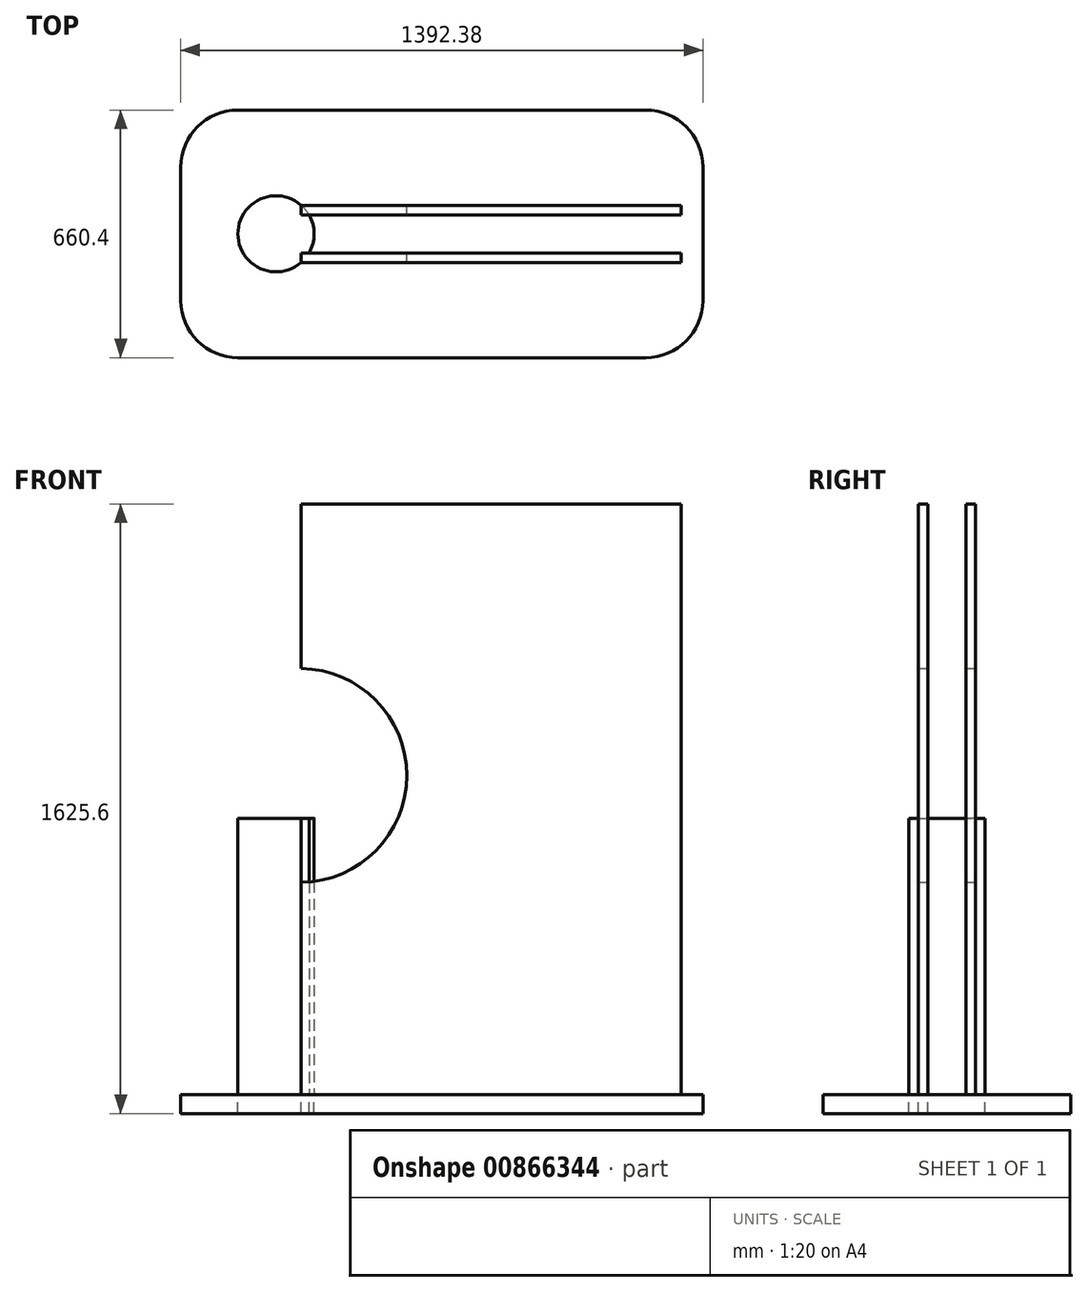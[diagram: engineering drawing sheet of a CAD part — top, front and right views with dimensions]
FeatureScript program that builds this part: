
annotation { "Feature Type Name" : "Feature", "Feature Type Description" : "" }
export const myFeature = defineFeature(function(context is Context, id is Id, definition is map)
    precondition{}
    {
        {
            var Q0;
            Q0=qCreatedBy(makeId("Front.planeOp"),FACE);
            var sketch = newSketch(context, id + "F1", { "sketchPlane" : qUnion([Q0])});
            skArc(sketch, "E0", {"start": v(32.8, 565.52) * mm, "mid": v(314.4, 850.7) * mm, "end": v(32.8, 1135.86) * mm});
            skLineSegment(sketch, "E1.bottom", {"start": v(32.8, 0) * mm, "end": v(1045.36, 0) * mm});
            skLineSegment(sketch, "E1.top", {"start": v(32.8, 1574.8) * mm, "end": v(1045.36, 1574.8) * mm});
            skLineSegment(sketch, "E1.left", {"start": v(32.8, 0) * mm, "end": v(32.8, 565.52) * mm});
            skLineSegment(sketch, "E1.right", {"start": v(1045.36, 0) * mm, "end": v(1045.36, 1574.8) * mm});
            skLineSegment(sketch, "E2.trimOffspring", {"start": v(32.8, 1135.86) * mm, "end": v(32.8, 1574.8) * mm});
            skSolve(sketch);
        }
        {
            var Q0;
            Q0=makeQuery(id+"F1.imprint","IMPRINT",FACE,{"disambiguationData":[TD([[makeQuery(id+"F1.imprint","IMPRINT",EDGE,{"derivedFrom":sQuery(id+"F1.wireOp",EDGE,"E0")}),-1.0]])]});
            extrude(context, id + "F2", {"entities" : qUnion([Q0]), "depth" : 152.4 * mm, "offsetDistance" : 25.4 * mm});
        }
        {
            var Q0;
            Q0=makeQuery(id+"F2.opExtrude","SWEPT_FACE",FACE,{"disambiguationData":[OSD([sQuery(id+"F1.wireOp",EDGE,"E1.top")])]});
            var sketch = newSketch(context, id + "F3", { "sketchPlane" : qUnion([Q0])});
            skLineSegment(sketch, "E3.bottom", {"start": v(32.8, -25.4) * mm, "end": v(1045.36, -25.4) * mm});
            skLineSegment(sketch, "E3.top", {"start": v(32.8, -127) * mm, "end": v(1045.36, -127) * mm});
            skLineSegment(sketch, "E3.left", {"start": v(32.8, -25.4) * mm, "end": v(32.8, -127) * mm});
            skLineSegment(sketch, "E3.right", {"start": v(1045.36, -25.4) * mm, "end": v(1045.36, -127) * mm});
            skSolve(sketch);
        }
        {
            var Q0;
            Q0=makeQuery(id+"F3.imprint","IMPRINT",FACE,{"disambiguationData":[TD([[makeQuery(id+"F3.imprint","IMPRINT",EDGE,{"derivedFrom":sQuery(id+"F3.wireOp",EDGE,"E3.bottom")}),-1.0]])]});
            extrude(context, id + "F4", {"entities" : qUnion([Q0]), "operationType" : NewBodyOperationType.REMOVE, "oppositeDirection" : true, "depth" : 1574.8 * mm, "offsetDistance" : 25.4 * mm});
        }
        {
            var Q0;
            {var subQ2=sQuery(id+"F1.wireOp",EDGE,"E1.bottom");Q0=makeQuery(id+"F4.boolean.opBoolean","SPLIT",FACE,{"disambiguationData":[TD([makeQuery(id+"F4.opExtrude","SWEPT_FACE",FACE,{"disambiguationData":[OSD([sQuery(id+"F3.wireOp",EDGE,"E3.top")])]})])],"derivedFrom":makeQuery(id+"F2.opExtrude","SWEPT_FACE",FACE,{"disambiguationData":[OSD([subQ2])]})});}
            var sketch = newSketch(context, id + "F5", { "sketchPlane" : qUnion([Q0])});
            skArc(sketch, "E4", {"start": v(32.8, 152.4) * mm, "mid": v(-136, 76.2) * mm, "end": v(32.8, 0) * mm});
            skCircle(sketch, "E5", {"center": v(-34.4, 76.2) * mm, "radius": 101.6 * mm});
            skSolve(sketch);
        }
        {
            var Q0;
            {var subQ1=sQuery(id+"F1.wireOp",EDGE,"E1.left");var subQ2=sQuery(id+"F1.wireOp",EDGE,"E1.bottom");var subQ3=sQuery(id+"F3.wireOp",EDGE,"E3.top");var subQ4=makeQuery(id+"F4.boolean.opBoolean","SPLIT",EDGE,{"disambiguationData":[TD([makeQuery(id+"F4.opExtrude","SWEPT_FACE",FACE,{"disambiguationData":[OSD([subQ3])]})])],"derivedFrom":makeQuery(id+"F2.opExtrude","SWEPT_EDGE",EDGE,{"disambiguationData":[OSD([subQ2,subQ1])]})});Q0=makeQuery(id+"F5.imprint","IMPRINT",FACE,{"disambiguationData":[TD([[makeQuery(id+"F5.imprint","IMPRINT",EDGE,{"derivedFrom":subQ4}),-1.0]])]});}
            extrude(context, id + "F6", {"entities" : qUnion([Q0]), "oppositeDirection" : true, "depth" : 736.6 * mm, "offsetDistance" : 25.4 * mm});
        }
        {
            var Q0;
            Q0=makeQuery(id+"F6.opExtrude","CAP_FACE",FACE,{"disambiguationData":[OSD([sQuery(id+"F1.wireOp",EDGE,"E1.bottom"),sQuery(id+"F1.wireOp",EDGE,"E1.left"),sQuery(id+"F3.wireOp",EDGE,"E3.top"),sQuery(id+"F5.wireOp",EDGE,"E5")])],"isStart":true});
            var sketch = newSketch(context, id + "F7", { "sketchPlane" : qUnion([Q0])});
            skLineSegment(sketch, "E6.bottom", {"start": v(-136, 406.4) * mm, "end": v(951.58, 406.4) * mm});
            skLineSegment(sketch, "E6.top", {"start": v(-136, -254) * mm, "end": v(951.58, -254) * mm});
            skLineSegment(sketch, "E6.left", {"start": v(-288.4, 254) * mm, "end": v(-288.4, -101.6) * mm});
            skLineSegment(sketch, "E6.right", {"start": v(1103.98, 254) * mm, "end": v(1103.98, -101.6) * mm});
            skPoint(sketch, "E7.visualSharp", {"position": v(-288.4, 406.4) * mm});
            skArc(sketch, "E7.filletArc", {"start": v(-136, 406.4) * mm, "mid": v(-243.76, 361.76) * mm, "end": v(-288.4, 254) * mm});
            skPoint(sketch, "E8.visualSharp", {"position": v(-288.4, -254) * mm});
            skArc(sketch, "E8.filletArc", {"start": v(-288.4, -101.6) * mm, "mid": v(-243.76, -209.36) * mm, "end": v(-136, -254) * mm});
            skPoint(sketch, "E9.visualSharp", {"position": v(1103.98, -254) * mm});
            skArc(sketch, "E9.filletArc", {"start": v(951.58, -254) * mm, "mid": v(1059.34, -209.36) * mm, "end": v(1103.98, -101.6) * mm});
            skPoint(sketch, "E10.visualSharp", {"position": v(1103.98, 406.4) * mm});
            skArc(sketch, "E10.filletArc", {"start": v(1103.98, 254) * mm, "mid": v(1059.34, 361.76) * mm, "end": v(951.58, 406.4) * mm});
            skSolve(sketch);
        }
        {
            var Q0;
            Q0=makeQuery(id+"F7.imprint","IMPRINT",FACE,{"disambiguationData":[TD([[makeQuery(id+"F7.imprint","IMPRINT",EDGE,{"derivedFrom":sQuery(id+"F7.wireOp",EDGE,"E6.bottom")}),-1.0]])]});
            extrude(context, id + "F8", {"entities" : qUnion([Q0]), "depth" : 50.8 * mm, "offsetDistance" : 25.4 * mm});
        }
        {
            var Q0;
            Q0=makeQuery(id+"F6.opExtrude","CAP_FACE",FACE,{"disambiguationData":[OSD([sQuery(id+"F1.wireOp",EDGE,"E1.bottom"),sQuery(id+"F1.wireOp",EDGE,"E1.left"),sQuery(id+"F3.wireOp",EDGE,"E3.top"),sQuery(id+"F5.wireOp",EDGE,"E5")])],"isStart":true});
            extrude(context, id + "F9", {"entities" : qUnion([Q0]), "depth" : 50.8 * mm, "offsetDistance" : 25.4 * mm});
        }
    });
